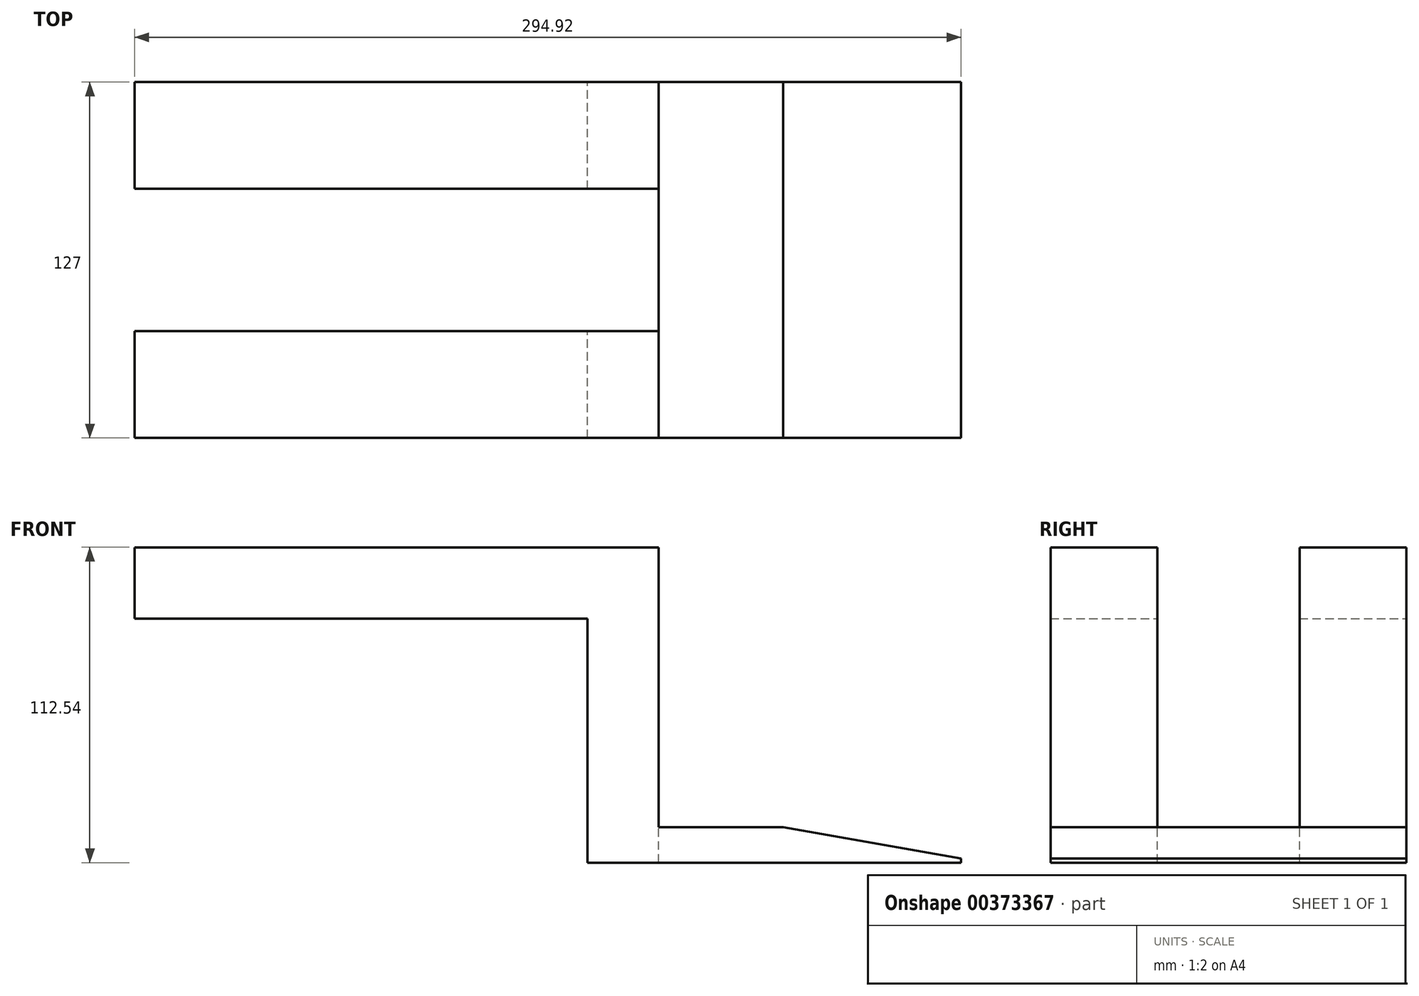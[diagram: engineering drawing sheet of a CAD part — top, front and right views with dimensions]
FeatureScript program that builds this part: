
annotation { "Feature Type Name" : "Feature", "Feature Type Description" : "" }
export const myFeature = defineFeature(function(context is Context, id is Id, definition is map)
    precondition{}
    {
        {
            var Q0;
            Q0=qCreatedBy(makeId("Front.planeOp"),FACE);
            var sketch = newSketch(context, id + "F0", { "sketchPlane" : qUnion([Q0])});
            skLineSegment(sketch, "E0", {"start": v(162.28, 0) * mm, "end": v(54.33, 0) * mm});
            skLineSegment(sketch, "E1", {"start": v(54.33, 0) * mm, "end": v(54.33, 99.84) * mm});
            skLineSegment(sketch, "E2", {"start": v(54.33, 99.84) * mm, "end": v(-132.64, 99.84) * mm});
            skLineSegment(sketch, "E3", {"start": v(-132.64, 99.84) * mm, "end": v(-132.64, 74.44) * mm});
            skLineSegment(sketch, "E4", {"start": v(-132.64, 74.44) * mm, "end": v(28.93, 74.44) * mm});
            skLineSegment(sketch, "E5", {"start": v(28.93, 74.44) * mm, "end": v(28.93, -12.7) * mm});
            skLineSegment(sketch, "E6", {"start": v(28.93, -12.7) * mm, "end": v(164.4, -12.7) * mm});
            skLineSegment(sketch, "E7", {"start": v(162.28, 0) * mm, "end": v(162.28, -12.7) * mm});
            skSolve(sketch);
        }
        {
            var Q0;
            Q0 = qSketchRegion(id + "F0", true);
            extrude(context, id + "F1", {"entities" : qUnion([Q0]), "depth" : 127 * mm});
        }
        {
            var Q0;
            Q0=makeQuery(id+"F1.opExtrude","SWEPT_FACE",FACE,{"disambiguationData":[OSD([sQuery(id+"F0.wireOp",EDGE,"E2")])]});
            var sketch = newSketch(context, id + "F2", { "sketchPlane" : qUnion([Q0])});
            skLineSegment(sketch, "E8.bottom", {"start": v(-132.64, -38.1) * mm, "end": v(54.33, -38.1) * mm});
            skLineSegment(sketch, "E8.top", {"start": v(-132.64, -88.9) * mm, "end": v(54.33, -88.9) * mm});
            skLineSegment(sketch, "E8.left", {"start": v(-132.64, -38.1) * mm, "end": v(-132.64, -88.9) * mm});
            skLineSegment(sketch, "E8.right", {"start": v(54.33, -38.1) * mm, "end": v(54.33, -88.9) * mm});
            skSolve(sketch);
        }
        {
            var Q0;
            Q0 = qSketchRegion(id + "F2", true);
            extrude(context, id + "F3", {"entities" : qUnion([Q0]), "operationType" : NewBodyOperationType.REMOVE, "endBound" : BoundingType.THROUGH_ALL, "oppositeDirection" : true, "depth" : 25.4 * mm});
        }
        {
            var Q0;
            Q0=makeQuery(id+"F1.opExtrude","SWEPT_EDGE",EDGE,{"disambiguationData":[OSD([sQuery(id+"F0.wireOp",EDGE,"E0"),sQuery(id+"F0.wireOp",EDGE,"E7")])]});
            chamfer(context, id + "F4", {"entities" : qUnion([Q0]), "chamferType" : ChamferType.OFFSET_ANGLE, "width" : 63.5 * mm, "oppositeDirection" : false, "angle" : 10 * degree, "tangentPropagation" : true});
        }
    });
